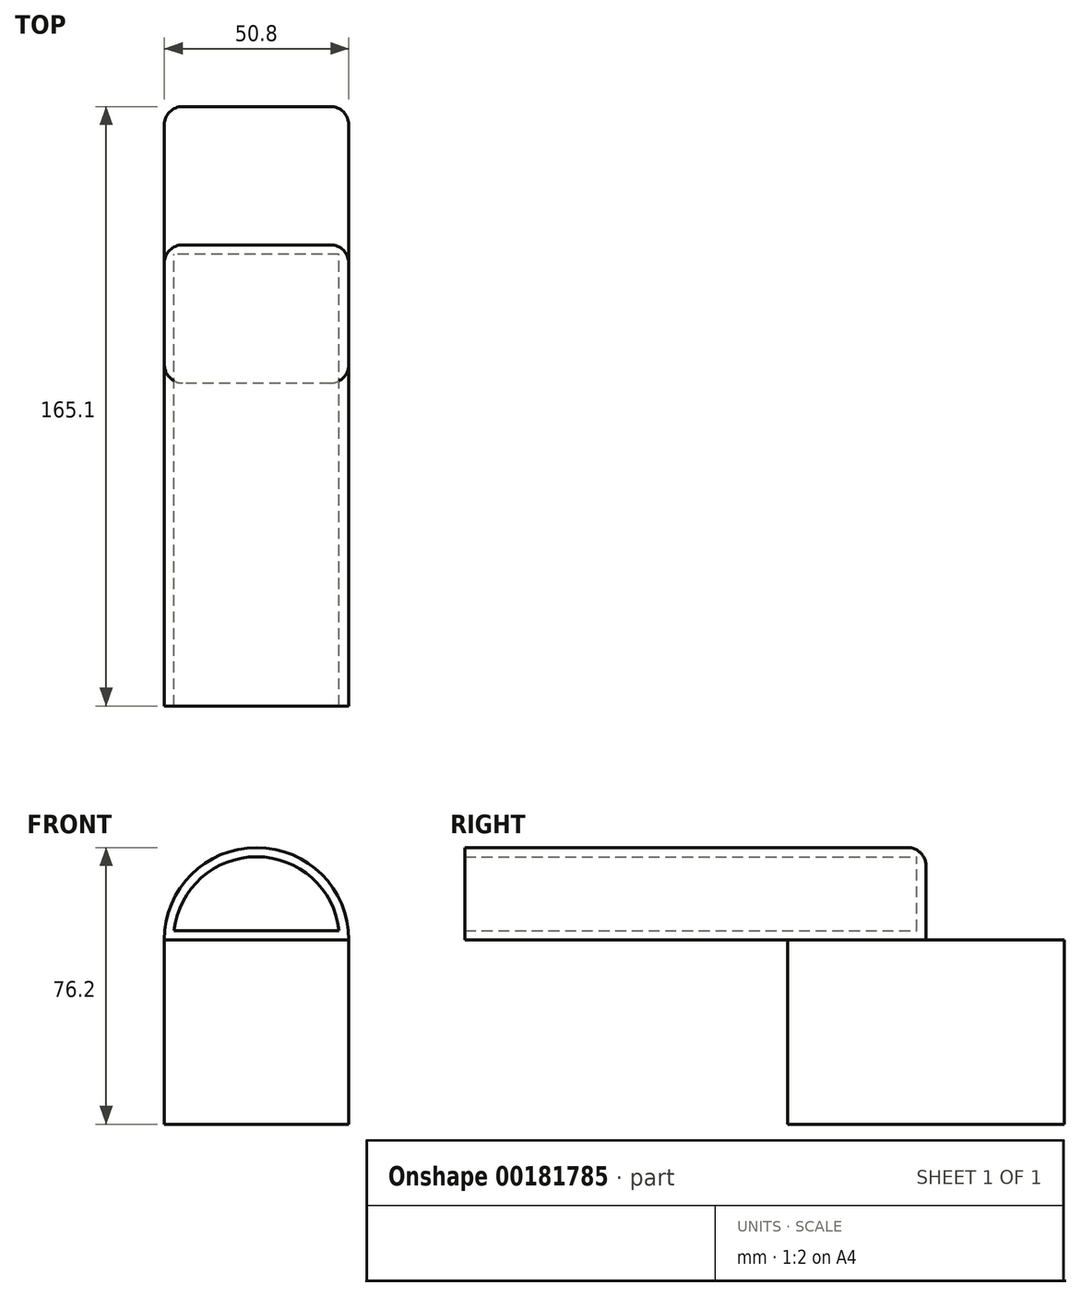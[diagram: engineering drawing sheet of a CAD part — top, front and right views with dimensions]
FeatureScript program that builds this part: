
annotation { "Feature Type Name" : "Feature", "Feature Type Description" : "" }
export const myFeature = defineFeature(function(context is Context, id is Id, definition is map)
    precondition{}
    {
        {
            var Q0;
            Q0=qCreatedBy(makeId("Front.planeOp"),FACE);
            var sketch = newSketch(context, id + "F0", { "sketchPlane" : qUnion([Q0])});
            skLineSegment(sketch, "E0.bottom", {"start": v(25.4, 25.4) * mm, "end": v(-25.4, 25.4) * mm});
            skLineSegment(sketch, "E0.top", {"start": v(25.4, -25.4) * mm, "end": v(-25.4, -25.4) * mm});
            skLineSegment(sketch, "E0.left", {"start": v(25.4, 25.4) * mm, "end": v(25.4, -25.4) * mm});
            skLineSegment(sketch, "E0.right", {"start": v(-25.4, 25.4) * mm, "end": v(-25.4, -25.4) * mm});
            skPoint(sketch, "E0.middle", {"position": v(0, 0) * mm});
            skCircle(sketch, "E1", {"center": v(0, 25.4) * mm, "radius": 25.4 * mm});
            skSolve(sketch);
        }
        {
            var Q0;
            Q0=makeQuery(id+"F0.imprint","IMPRINT",FACE,{"disambiguationData":[TD([[makeQuery(id+"F0.imprint","IMPRINT",EDGE,{"derivedFrom":sQuery(id+"F0.wireOp",EDGE,"E0.top")}),-1.0]])]});
            var Q1;
            {var subQ0=sQuery(id+"F0.wireOp",EDGE,"E0.bottom");Q1=makeQuery(id+"F0.imprint","IMPRINT",FACE,{"disambiguationData":[TD([[makeQuery(id+"F0.imprint","IMPRINT",EDGE,{"derivedFrom":subQ0}),1.0]])]});}
            extrude(context, id + "F1", {"entities" : qUnion([Q0, Q1]), "endBound" : BoundingType.SYMMETRIC, "depth" : 76.2 * mm});
        }
        {
            var Q0;
            {var subQ0=sQuery(id+"F0.wireOp",EDGE,"E0.bottom");Q0=makeQuery(id+"F0.imprint","IMPRINT",FACE,{"disambiguationData":[TD([[makeQuery(id+"F0.imprint","IMPRINT",EDGE,{"derivedFrom":subQ0}),-1.0]])]});}
            extrude(context, id + "F2", {"entities" : qUnion([Q0]), "depth" : 127 * mm});
        }
        {
            var Q0;
            Q0=makeQuery(id+"F2.opExtrude","CAP_FACE",FACE,{"disambiguationData":[OSD([sQuery(id+"F0.wireOp",EDGE,"E0.bottom"),sQuery(id+"F0.wireOp",EDGE,"E1")])],"isStart":false});
            shell(context, id + "F3", {"entities" : qUnion([Q0]), "thickness" : 2.54 * mm});
        }
        {
            var Q0;
            Q0=makeQuery(id+"F1.opExtrude","CAP_EDGE",EDGE,{"disambiguationData":[OSD([sQuery(id+"F0.wireOp",EDGE,"E0.right")])],"isStart":false});
            var Q1;
            Q1=makeQuery(id+"F1.opExtrude","CAP_EDGE",EDGE,{"disambiguationData":[OSD([sQuery(id+"F0.wireOp",EDGE,"E0.left")])],"isStart":false});
            var Q2;
            Q2=makeQuery(id+"F1.opExtrude","CAP_EDGE",EDGE,{"disambiguationData":[OSD([sQuery(id+"F0.wireOp",EDGE,"E0.left")])],"isStart":true});
            var Q3;
            Q3=makeQuery(id+"F1.opExtrude","CAP_EDGE",EDGE,{"disambiguationData":[OSD([sQuery(id+"F0.wireOp",EDGE,"E0.right")])],"isStart":true});
            var Q4;
            Q4=makeQuery(id+"F2.opExtrude","CAP_EDGE",EDGE,{"disambiguationData":[OSD([sQuery(id+"F0.wireOp",EDGE,"E1")])],"isStart":true});
            fillet(context, id + "F4", {"entities" : qUnion([Q0, Q1, Q2, Q3, Q4]), "radius" : 5.08 * mm, "tangentPropagation" : true, "allowEdgeOverflow" : false});
        }
    });
